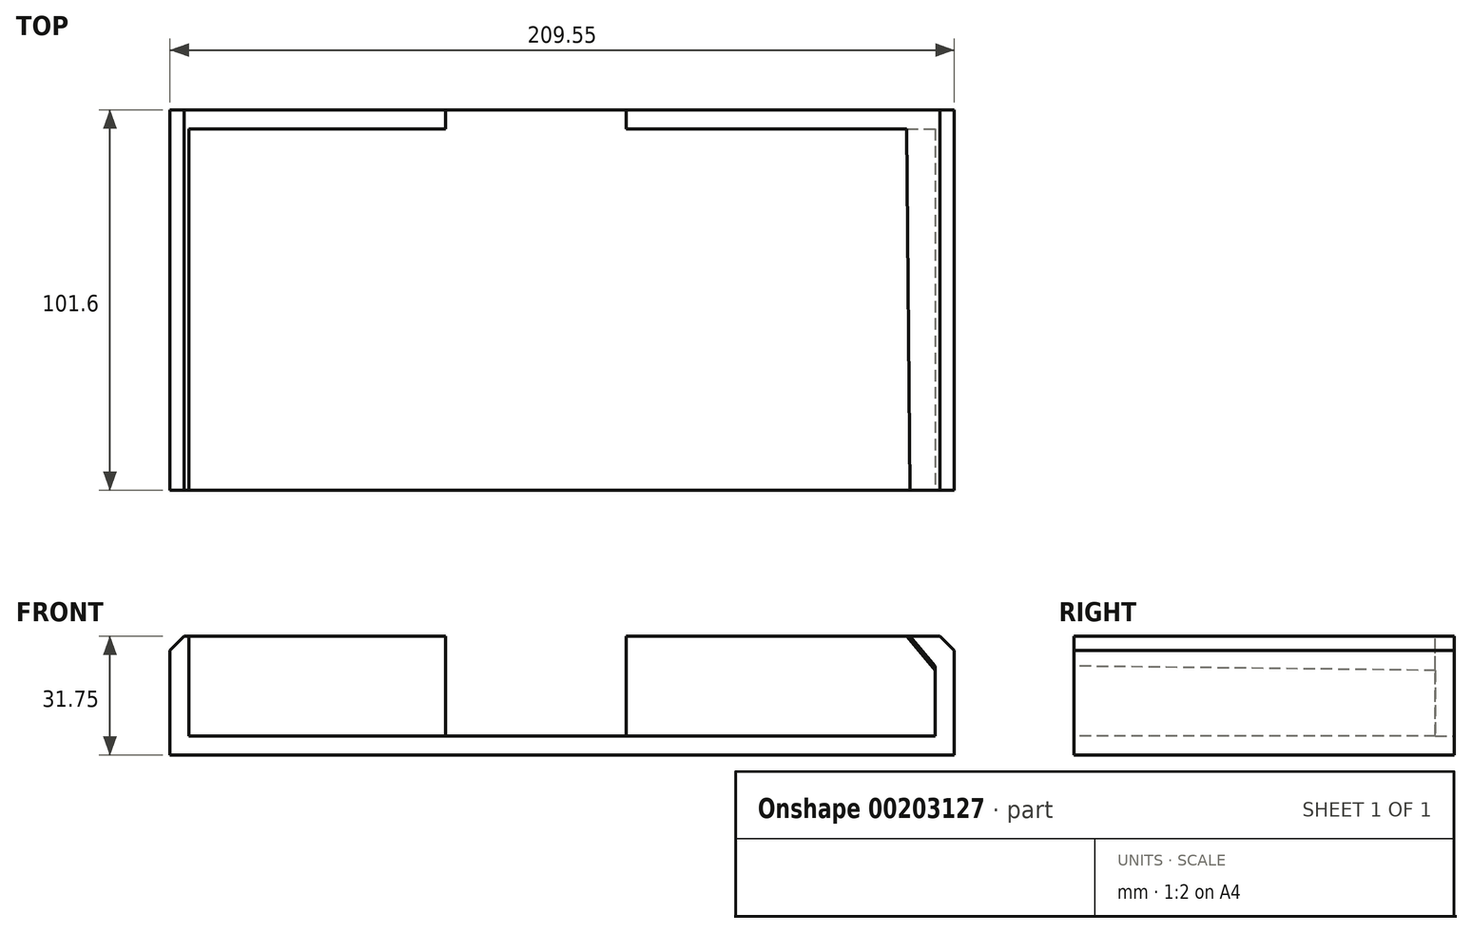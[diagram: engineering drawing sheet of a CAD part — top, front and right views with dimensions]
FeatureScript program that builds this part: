
annotation { "Feature Type Name" : "Feature", "Feature Type Description" : "" }
export const myFeature = defineFeature(function(context is Context, id is Id, definition is map)
    precondition{}
    {
        {
            var Q0;
            Q0=qCreatedBy(makeId("Top.planeOp"),FACE);
            var sketch = newSketch(context, id + "F0", { "sketchPlane" : qUnion([Q0])});
            skLineSegment(sketch, "E0.bottom", {"start": v(-113.45, 68.37) * mm, "end": v(96.1, 68.37) * mm});
            skLineSegment(sketch, "E0.top", {"start": v(-113.45, -33.23) * mm, "end": v(96.1, -33.23) * mm});
            skLineSegment(sketch, "E0.left", {"start": v(-113.45, 68.37) * mm, "end": v(-113.45, -33.23) * mm});
            skLineSegment(sketch, "E0.right", {"start": v(96.1, 68.37) * mm, "end": v(96.1, -33.23) * mm});
            skSolve(sketch);
        }
        {
            var Q0;
            Q0=makeQuery(id+"F0.imprint","IMPRINT",FACE,{"disambiguationData":[TD([[makeQuery(id+"F0.imprint","IMPRINT",EDGE,{"derivedFrom":sQuery(id+"F0.wireOp",EDGE,"E0.bottom")}),-1.0]])]});
            extrude(context, id + "F1", {"entities" : qUnion([Q0]), "depth" : 31.75 * mm});
        }
        {
            var Q0;
            Q0=makeQuery(id+"F1.opExtrude","SWEPT_FACE",FACE,{"disambiguationData":[OSD([sQuery(id+"F0.wireOp",EDGE,"E0.top")])]});
            var sketch = newSketch(context, id + "F2", { "sketchPlane" : qUnion([Q0])});
            skLineSegment(sketch, "E1.top", {"start": v(-108.37, 5.08) * mm, "end": v(91.02, 5.08) * mm});
            skLineSegment(sketch, "E1.left", {"start": v(-108.37, 26.67) * mm, "end": v(-108.37, 5.08) * mm});
            skLineSegment(sketch, "E1.right", {"start": v(91.02, 26.67) * mm, "end": v(91.02, 5.08) * mm});
            skLineSegment(sketch, "E2", {"start": v(-103.29, 31.75) * mm, "end": v(85.94, 31.75) * mm});
            skLineSegment(sketch, "E3", {"start": v(-108.37, 26.67) * mm, "end": v(-103.29, 31.75) * mm});
            skLineSegment(sketch, "E4", {"start": v(91.02, 26.67) * mm, "end": v(85.94, 31.75) * mm});
            skLineSegment(sketch, "E5", {"start": v(-108.37, 26.67) * mm, "end": v(-108.37, 31.75) * mm});
            skLineSegment(sketch, "E6", {"start": v(91.02, 26.67) * mm, "end": v(91.02, 31.75) * mm});
            skSolve(sketch);
        }
        {
            var Q0;
            Q0=makeQuery(id+"F2.imprint","IMPRINT",FACE,{"disambiguationData":[TD([[makeQuery(id+"F2.imprint","IMPRINT",EDGE,{"derivedFrom":sQuery(id+"F2.wireOp",EDGE,"E1.top")}),1.0]])]});
            var Q1;
            {var subQ0=sQuery(id+"F2.wireOp",EDGE,"E4");Q1=makeQuery(id+"F2.imprint","IMPRINT",FACE,{"disambiguationData":[TD([[makeQuery(id+"F2.imprint","IMPRINT",EDGE,{"derivedFrom":subQ0}),-1.0]])]});}
            var Q2;
            {var subQ0=sQuery(id+"F2.wireOp",EDGE,"E3");Q2=makeQuery(id+"F2.imprint","IMPRINT",FACE,{"disambiguationData":[TD([[makeQuery(id+"F2.imprint","IMPRINT",EDGE,{"derivedFrom":subQ0}),1.0]])]});}
            extrude(context, id + "F3", {"entities" : qUnion([Q0, Q1, Q2]), "operationType" : NewBodyOperationType.REMOVE, "oppositeDirection" : true, "depth" : 96.52 * mm});
        }
        {
            var Q0;
            Q0=makeQuery(id+"F1.opExtrude","SWEPT_FACE",FACE,{"disambiguationData":[OSD([sQuery(id+"F0.wireOp",EDGE,"E0.bottom")])]});
            var sketch = newSketch(context, id + "F4", { "sketchPlane" : qUnion([Q0])});
            skPoint(sketch, "E7.endSnap0", {"position": v(113.45, 15.88) * mm});
            skLineSegment(sketch, "E8.top", {"start": v(-8.47, 5.08) * mm, "end": v(39.79, 5.08) * mm});
            skLineSegment(sketch, "E9", {"start": v(-8.47, 5.08) * mm, "end": v(-8.47, 31.75) * mm});
            skLineSegment(sketch, "E10", {"start": v(39.79, 5.08) * mm, "end": v(39.79, 31.75) * mm});
            skLineSegment(sketch, "E11", {"start": v(39.79, 31.75) * mm, "end": v(-8.47, 31.75) * mm});
            skSolve(sketch);
        }
        {
            var Q0;
            Q0=makeQuery(id+"F4.imprint","IMPRINT",FACE,{"disambiguationData":[TD([[makeQuery(id+"F4.imprint","IMPRINT",EDGE,{"derivedFrom":sQuery(id+"F4.wireOp",EDGE,"E8.top")}),1.0]])]});
            extrude(context, id + "F5", {"entities" : qUnion([Q0]), "operationType" : NewBodyOperationType.REMOVE, "oppositeDirection" : true, "depth" : 5.08 * mm});
        }
        {
            var Q0;
            {var subQ0=sQuery(id+"F2.wireOp",EDGE,"E6");var subQ1=sQuery(id+"F2.wireOp",EDGE,"E1.right");var subQ2=sQuery(id+"F2.wireOp",EDGE,"E1.top");var subQ3=sQuery(id+"F0.wireOp",EDGE,"E0.top");Q0=makeQuery(id+"F5.boolean.opBoolean","SPLIT",FACE,{"disambiguationData":[TD([makeQuery(id+"F5.opExtrude","SWEPT_FACE",FACE,{"disambiguationData":[OSD([sQuery(id+"F4.wireOp",EDGE,"E9")])]})])],"derivedFrom":makeQuery(id+"F3.boolean.opBoolean","COPY",FACE,{"derivedFrom":makeQuery(id+"F3.opExtrude","CAP_FACE",FACE,{"disambiguationData":[OSD([subQ3,subQ2,sQuery(id+"F2.wireOp",EDGE,"E1.left"),subQ1,sQuery(id+"F2.wireOp",EDGE,"E2"),sQuery(id+"F2.wireOp",EDGE,"E5"),subQ0])],"isStart":false})})});}
            var sketch = newSketch(context, id + "F6", { "sketchPlane" : qUnion([Q0])});
            skLineSegment(sketch, "E12", {"start": v(91.02, 31.75) * mm, "end": v(91.02, 22.6) * mm});
            skPoint(sketch, "E13", {"position": v(91.02, 5.08) * mm});
            skLineSegment(sketch, "E14", {"start": v(91.02, 22.6) * mm, "end": v(83.35, 31.75) * mm});
            skSolve(sketch);
        }
        {
            var Q0;
            Q0=makeQuery(id+"F1.opExtrude","SWEPT_FACE",FACE,{"disambiguationData":[OSD([sQuery(id+"F0.wireOp",EDGE,"E0.top")])]});
            var sketch = newSketch(context, id + "F7", { "sketchPlane" : qUnion([Q0])});
            skLineSegment(sketch, "E15", {"start": v(91.02, 31.75) * mm, "end": v(91.02, 23.75) * mm});
            skPoint(sketch, "E16", {"position": v(91.02, 5.08) * mm});
            skLineSegment(sketch, "E17", {"start": v(91.02, 23.75) * mm, "end": v(84.31, 31.75) * mm});
            skLineSegment(sketch, "E18", {"start": v(84.31, 31.75) * mm, "end": v(91.02, 31.75) * mm});
            skSolve(sketch);
        }
        {
            var Q1;
            {var subQ0=sQuery(id+"F6.wireOp",EDGE,"E12");Q1=makeQuery(id+"F6.imprint","IMPRINT",FACE,{"disambiguationData":[TD([[makeQuery(id+"F6.imprint","IMPRINT",EDGE,{"derivedFrom":subQ0}),-1.0]])]});}
            var Q2;
            Q2=makeQuery(id+"F7.imprint","IMPRINT",FACE,{"disambiguationData":[TD([[makeQuery(id+"F7.imprint","IMPRINT",EDGE,{"derivedFrom":sQuery(id+"F7.wireOp",EDGE,"E15")}),-1.0]])]});
            loft(context, id + "F8", {"operationType" : NewBodyOperationType.ADD, "sheetProfilesArray" : [{ "sheetProfileEntities" : qUnion([Q1]) }, { "sheetProfileEntities" : qUnion([Q2]) }]});
        }
        {
            var Q0;
            Q0=makeQuery(id+"F1.opExtrude","SWEPT_FACE",FACE,{"disambiguationData":[OSD([sQuery(id+"F0.wireOp",EDGE,"E0.left")])]});
            cPlane(context, id + "F9", {"entities" : qUnion([Q0]), "cplaneType" : CPlaneType.OFFSET, "offset" : 104.77 * mm, "oppositeDirection" : true, "width" : 152.4 * mm, "height" : 152.4 * mm});
        }
        {
            var Q0;
            Q0=makeQuery(id+"F1.opExtrude","CAP_EDGE",EDGE,{"disambiguationData":[OSD([sQuery(id+"F0.wireOp",EDGE,"E0.left")])],"isStart":false});
            var Q1;
            Q1=makeQuery(id+"F1.opExtrude","CAP_EDGE",EDGE,{"disambiguationData":[OSD([sQuery(id+"F0.wireOp",EDGE,"E0.right")])],"isStart":false});
            chamfer(context, id + "F10", {"entities" : qUnion([Q0, Q1]), "width" : 3.8 * mm, "tangentPropagation" : true});
        }
    });
